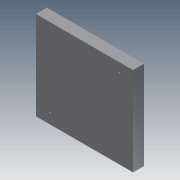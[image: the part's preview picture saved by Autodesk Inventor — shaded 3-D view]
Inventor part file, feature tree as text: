
AUTODESK INVENTOR PART (.ipt)
format: ipt  version: 2011 (Build 150239000, 239)  size: 228,864 bytes
history: native  units: in
note: dims shown in document units (in); Inventor stores cm internally (conversion verified against a paired STEP export)
features: extrude x19, sketch x19
ambient origin geometry x8: Origin, YZ Plane, XZ Plane, XY Plane, X Axis, Y Axis, Z Axis, Center Point
bodies: Solid1 (feature_tree)
feature tree (38):
  extrude  "Extrusion1"  Depth=1.9685in
  extrude  "Extrusion2"  Depth=0.375in TaperAngle=0.0deg
  extrude  "Extrusion3"  Depth=0.5906in
  extrude  "Extrusion4"  Depth=0.5906in
  extrude  "Extrusion5"  Depth=0.7874in
  extrude  "Extrusion6"  Depth=0.7874in
  extrude  "Extrusion7"  Depth=0.0394in
  extrude  "Extrusion8"  Depth=1.0in TaperAngle=0.0deg
  extrude  "Extrusion9"  Depth=0.0625in
  extrude  "Extrusion10"  Depth=0.125in TaperAngle=0.0deg
  extrude  "Extrusion11"  Depth=0.05in TaperAngle=0.0deg
  extrude  "Extrusion12"  Depth=0.05in TaperAngle=0.0deg
  extrude  "Extrusion13"  Depth=0.05in TaperAngle=0.0deg
  extrude  "Extrusion14"  Depth=0.0394in TaperAngle=0.0deg
  extrude  "Extrusion15"  Depth=0.0394in TaperAngle=0.0deg
  extrude  "Extrusion16"  Depth=0.0787in TaperAngle=0.0deg
  extrude  "Extrusion17"  [1 undecoded]
  extrude  "Extrusion18"  [1 undecoded]
  extrude  "Extrusion19"  [1 undecoded]
  sketch  "Sketch1"  dims[d0=1.9685in d1=1.9685in]
  sketch  "Sketch2"  dims[d2=0.125in d3=0.0in d4=0.375in d5=0.0in]
  sketch  "Sketch3"  dims[d6=0.125in d7=0.5906in]
  sketch  "Sketch4"  dims[d8=0.125in d9=0.5906in]
  sketch  "Sketch5"  dims[d10=0.375in d11=0.0in d12=0.7874in]
  sketch  "Sketch6"  dims[d13=0.1969in d14=0.7874in]
  sketch  "Sketch7"  dims[d15=0.1969in d16=0.0394in]
  sketch  "Sketch8"  dims[d17=0.0394in d18=1.0in d19=0.0in]
  sketch  "Sketch9"  dims[d20=0.0625in d21=0.0625in]
  sketch  "Sketch10"  dims[d22=1.0in d23=0.0in d24=0.125in d25=0.0in]
  sketch  "Sketch11"  dims[d26=0.05in d27=0.0in d28=0.05in d29=0.0in]
  sketch  "Sketch12"  dims[d30=0.125in d31=0.0in d32=0.05in d33=0.0in]
  sketch  "Sketch13"  dims[d34=0.05in d35=0.0in d36=0.05in d37=0.0in]
  sketch  "Sketch14"  dims[d38=0.05in d39=0.0in d40=0.0394in d41=0.0in]
  sketch  "Sketch15"  dims[d42=0.0394in d43=0.0in d44=0.0394in d45=0.0in]
  sketch  "Sketch16"  dims[d46=0.0787in d47=0.0in d48=0.0787in d49=0.0in]
  sketch  "Sketch17"  dims[d50=0.125in d51=0.0in]
  sketch  "Sketch18"
  sketch  "Sketch19"
note: 3 required parameter values undecoded (feature->parameter linkage not recoverable at this tier; creation-order binding heuristic only, values carry confidence <= 0.55)
